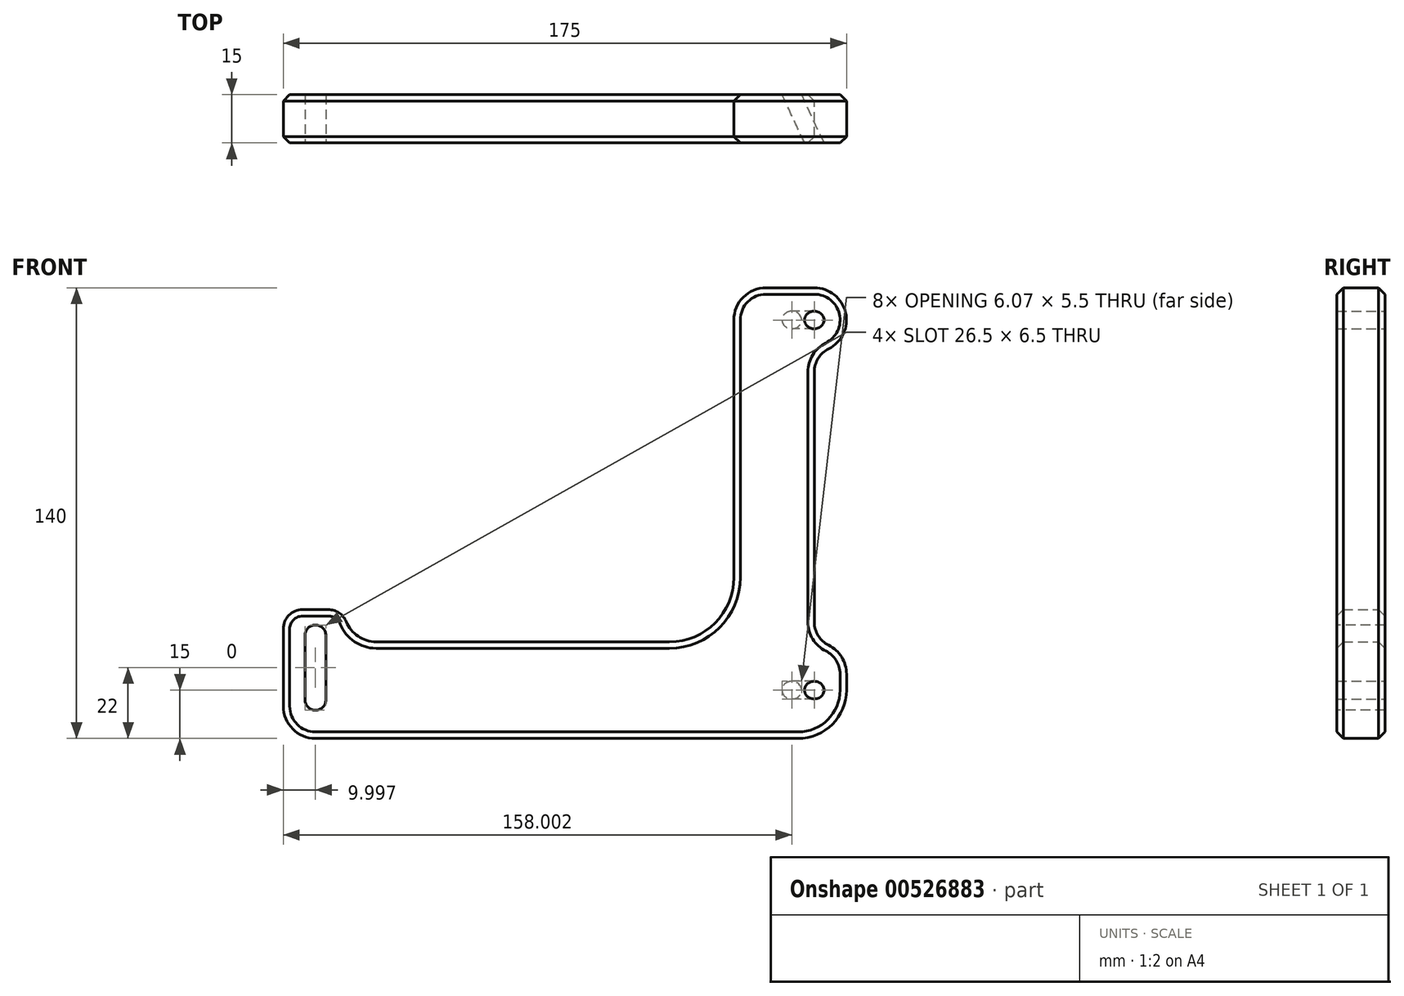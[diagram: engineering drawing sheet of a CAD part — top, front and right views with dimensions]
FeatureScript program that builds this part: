
annotation { "Feature Type Name" : "Feature", "Feature Type Description" : "" }
export const myFeature = defineFeature(function(context is Context, id is Id, definition is map)
    precondition{}
    {
        {
            var Q0;
            Q0=qCreatedBy(makeId("Front.planeOp"),FACE);
            var sketch = newSketch(context, id + "F0", { "sketchPlane" : qUnion([Q0])});
            skLineSegment(sketch, "E0", {"start": v(-2.83, 90) * mm, "end": v(-2.83, 0) * mm});
            skLineSegment(sketch, "E1", {"start": v(-2.84, 110) * mm, "end": v(-17.83, 110) * mm});
            skLineSegment(sketch, "E2", {"start": v(-27.83, 100) * mm, "end": v(-27.83, 20) * mm});
            skLineSegment(sketch, "E3", {"start": v(-47.83, 0) * mm, "end": v(-147.83, 0) * mm});
            skLineSegment(sketch, "E4", {"start": v(-153.83, 10) * mm, "end": v(-161.83, 10) * mm});
            skLineSegment(sketch, "E5", {"start": v(-167.83, 4) * mm, "end": v(-167.83, -20) * mm});
            skLineSegment(sketch, "E6", {"start": v(-157.83, -30) * mm, "end": v(-7.83, -30) * mm});
            skLineSegment(sketch, "E7", {"start": v(7.17, -15) * mm, "end": v(7.17, -10) * mm});
            skLineSegment(sketch, "E8", {"start": v(-2.83, 0) * mm, "end": v(-2.83, 0) * mm});
            skPoint(sketch, "E9.visualSharp", {"position": v(-27.83, 110) * mm});
            skArc(sketch, "E9.filletArc", {"start": v(-17.83, 110) * mm, "mid": v(-24.9, 107.07) * mm, "end": v(-27.83, 100) * mm});
            skPoint(sketch, "E10.visualSharp", {"position": v(7.16, 110) * mm});
            skLineSegment(sketch, "E10.filletArc", {"start": v(7.16, 110) * mm, "end": v(7.16, 110) * mm});
            skPoint(sketch, "E11.visualSharp", {"position": v(7.16, 90) * mm});
            skPoint(sketch, "E12.visualSharp", {"position": v(-2.83, 90) * mm});
            skPoint(sketch, "E13.visualSharp", {"position": v(-2.83, 0) * mm});
            skPoint(sketch, "E14.visualSharp", {"position": v(7.17, 0) * mm});
            skPoint(sketch, "E15.visualSharp", {"position": v(7.17, -30) * mm});
            skArc(sketch, "E15.filletArc", {"start": v(-7.83, -30) * mm, "mid": v(2.77, -25.6) * mm, "end": v(7.17, -15) * mm});
            skPoint(sketch, "E16.visualSharp", {"position": v(-27.83, 0) * mm});
            skArc(sketch, "E16.filletArc", {"start": v(-47.83, 0) * mm, "mid": v(-33.7, 5.86) * mm, "end": v(-27.83, 20) * mm});
            skPoint(sketch, "E17.visualSharp", {"position": v(-147.83, 0) * mm});
            skPoint(sketch, "E18.visualSharp", {"position": v(-147.83, 10) * mm});
            skPoint(sketch, "E19.visualSharp", {"position": v(-167.83, 10) * mm});
            skArc(sketch, "E19.filletArc", {"start": v(-161.83, 10) * mm, "mid": v(-166.08, 8.24) * mm, "end": v(-167.83, 4) * mm});
            skPoint(sketch, "E20.visualSharp", {"position": v(-167.83, -30) * mm});
            skArc(sketch, "E20.filletArc", {"start": v(-167.83, -20) * mm, "mid": v(-164.9, -27.07) * mm, "end": v(-157.83, -30) * mm});
            skLineSegment(sketch, "E21", {"start": v(-147.83, 4) * mm, "end": v(-147.83, 4) * mm});
            skLineSegment(sketch, "E22", {"start": v(-2.84, 90) * mm, "end": v(-2.83, 90) * mm});
            skLineSegment(sketch, "E23", {"start": v(7.16, 100) * mm, "end": v(7.16, 100) * mm});
            skArc(sketch, "E24.filletArc", {"start": v(7.17, -10) * mm, "mid": v(4.24, -2.93) * mm, "end": v(-2.83, 0) * mm});
            skArc(sketch, "E25.filletArc", {"start": v(-2.84, 90) * mm, "mid": v(4.23, 92.93) * mm, "end": v(7.16, 100) * mm});
            skArc(sketch, "E26.filletArc", {"start": v(7.16, 100) * mm, "mid": v(4.23, 107.07) * mm, "end": v(-2.84, 110) * mm});
            skLineSegment(sketch, "E27", {"start": v(-147.83, 0) * mm, "end": v(-147.83, 10) * mm});
            skLineSegment(sketch, "E28", {"start": v(-153.83, 10) * mm, "end": v(-147.83, 10) * mm});
            skSolve(sketch);
        }
        {
            var Q0;
            Q0=makeQuery(id+"F0.imprint","IMPRINT",FACE,{"disambiguationData":[TD([[makeQuery(id+"F0.imprint","IMPRINT",EDGE,{"derivedFrom":sQuery(id+"F0.wireOp",EDGE,"E0")}),-1.0]])]});
            extrude(context, id + "F1", {"entities" : qUnion([Q0]), "depth" : 15 * mm, "offsetDistance" : 25 * mm});
        }
        {
            var Q0;
            Q0=makeQuery(id+"F1.opExtrude","CAP_FACE",FACE,{"disambiguationData":[OSD([sQuery(id+"F0.wireOp",EDGE,"E0"),sQuery(id+"F0.wireOp",EDGE,"J42z8YOY-xz5I-P0zV-WpF7-1QvDG5DtMwlX"),sQuery(id+"F0.wireOp",EDGE,"2vvke65l-5Rt1-P847-MWuo-q8DSQjlYU5eZ"),sQuery(id+"F0.wireOp",EDGE,"E1"),sQuery(id+"F0.wireOp",EDGE,"E2"),sQuery(id+"F0.wireOp",EDGE,"E3"),sQuery(id+"F0.wireOp",EDGE,"E4"),sQuery(id+"F0.wireOp",EDGE,"E5"),sQuery(id+"F0.wireOp",EDGE,"E6"),sQuery(id+"F0.wireOp",EDGE,"E7"),sQuery(id+"F0.wireOp",EDGE,"E8"),sQuery(id+"F0.wireOp",EDGE,"E9.filletArc"),sQuery(id+"F0.wireOp",EDGE,"E10.filletArc"),sQuery(id+"F0.wireOp",EDGE,"E11.filletArc"),sQuery(id+"F0.wireOp",EDGE,"E12.filletArc"),sQuery(id+"F0.wireOp",EDGE,"E13.filletArc"),sQuery(id+"F0.wireOp",EDGE,"E14.filletArc"),sQuery(id+"F0.wireOp",EDGE,"E15.filletArc"),sQuery(id+"F0.wireOp",EDGE,"E16.filletArc"),sQuery(id+"F0.wireOp",EDGE,"E19.filletArc"),sQuery(id+"F0.wireOp",EDGE,"E20.filletArc"),sQuery(id+"F0.wireOp",EDGE,"E21"),sQuery(id+"F0.wireOp",EDGE,"44b101ba-7efd-4e18-aab7-cb58494b7f6b.filletArc"),sQuery(id+"F0.wireOp",EDGE,"d437f479-9b5c-4e56-8808-f89f6181e417.filletArc")])],"isStart":false});
            var sketch = newSketch(context, id + "F2", { "sketchPlane" : qUnion([Q0])});
            skArc(sketch, "E29", {"start": v(-154.58, 2) * mm, "mid": v(-157.83, 5.25) * mm, "end": v(-161.08, 2) * mm});
            skArc(sketch, "E30", {"start": v(-161.08, -18) * mm, "mid": v(-157.83, -21.25) * mm, "end": v(-154.58, -18) * mm});
            skLineSegment(sketch, "E31", {"start": v(-161.08, 2) * mm, "end": v(-161.08, -18) * mm});
            skLineSegment(sketch, "E32", {"start": v(-154.58, 2) * mm, "end": v(-154.58, -18) * mm});
            skSolve(sketch);
        }
        {
            var Q0;
            Q0 = qSketchRegion(id + "F2", true);
            extrude(context, id + "F3", {"entities" : qUnion([Q0]), "operationType" : NewBodyOperationType.REMOVE, "oppositeDirection" : true, "depth" : 20 * mm, "offsetDistance" : 25 * mm});
        }
        {
            var Q0;
            Q0=makeQuery(id+"F1.opExtrude","CAP_FACE",FACE,{"disambiguationData":[OSD([sQuery(id+"F0.wireOp",EDGE,"E0"),sQuery(id+"F0.wireOp",EDGE,"J42z8YOY-xz5I-P0zV-WpF7-1QvDG5DtMwlX"),sQuery(id+"F0.wireOp",EDGE,"2vvke65l-5Rt1-P847-MWuo-q8DSQjlYU5eZ"),sQuery(id+"F0.wireOp",EDGE,"E1"),sQuery(id+"F0.wireOp",EDGE,"E2"),sQuery(id+"F0.wireOp",EDGE,"E3"),sQuery(id+"F0.wireOp",EDGE,"E4"),sQuery(id+"F0.wireOp",EDGE,"E5"),sQuery(id+"F0.wireOp",EDGE,"E6"),sQuery(id+"F0.wireOp",EDGE,"E7"),sQuery(id+"F0.wireOp",EDGE,"E8"),sQuery(id+"F0.wireOp",EDGE,"E9.filletArc"),sQuery(id+"F0.wireOp",EDGE,"E10.filletArc"),sQuery(id+"F0.wireOp",EDGE,"E11.filletArc"),sQuery(id+"F0.wireOp",EDGE,"E12.filletArc"),sQuery(id+"F0.wireOp",EDGE,"E13.filletArc"),sQuery(id+"F0.wireOp",EDGE,"E14.filletArc"),sQuery(id+"F0.wireOp",EDGE,"E15.filletArc"),sQuery(id+"F0.wireOp",EDGE,"E16.filletArc"),sQuery(id+"F0.wireOp",EDGE,"E19.filletArc"),sQuery(id+"F0.wireOp",EDGE,"E20.filletArc"),sQuery(id+"F0.wireOp",EDGE,"44b101ba-7efd-4e18-aab7-cb58494b7f6b.filletArc"),sQuery(id+"F0.wireOp",EDGE,"d437f479-9b5c-4e56-8808-f89f6181e417.filletArc")])],"isStart":false});
            var sketch = newSketch(context, id + "F4", { "sketchPlane" : qUnion([Q0])});
            skCircle(sketch, "E33", {"center": v(-2.83, 100) * mm, "radius": 3 * mm});
            skCircle(sketch, "E34", {"center": v(-2.83, -15) * mm, "radius": 3 * mm});
            skSolve(sketch);
        }
        {
            var Q0;
            Q0=makeQuery(id+"F1.opExtrude","CAP_EDGE",EDGE,{"disambiguationData":[OSD([sQuery(id+"F0.wireOp",EDGE,"E2")])],"isStart":false});
            cPlane(context, id + "F5", {"entities" : qUnion([Q0]), "cplaneType" : CPlaneType.LINE_ANGLE, "offset" : 25 * mm, "angle" : 65 * degree, "width" : 150 * mm, "height" : 150 * mm});
        }
        {
            var Q0;
            Q0=qCreatedBy(id+"F5.planeOp",FACE);
            cPlane(context, id + "F6", {"entities" : qUnion([Q0]), "cplaneType" : CPlaneType.OFFSET, "offset" : 25 * mm, "width" : 150 * mm, "height" : 150 * mm});
        }
        {
            var Q0;
            Q0=qCreatedBy(id+"F6.planeOp",FACE);
            var sketch = newSketch(context, id + "F7", { "sketchPlane" : qUnion([Q0])});
            skPoint(sketch, "E35.0", {"position": v(8.9, 100) * mm});
            skPoint(sketch, "E36.0", {"position": v(8.9, -15) * mm});
            skSolve(sketch);
        }
        {
            var Q0;
            Q0=sQuery(id+"F7.wireOp",VERTEX,"E35.0");
            var Q1;
            Q1=sQuery(id+"F7.wireOp",VERTEX,"E36.0");
            var Q2;
            Q2=makeQuery(id+"F1.opExtrude","SWEPT_BODY",BODY,{"disambiguationData":[OSD([sQuery(id+"F0.wireOp",EDGE,"E0"),sQuery(id+"F0.wireOp",EDGE,"J42z8YOY-xz5I-P0zV-WpF7-1QvDG5DtMwlX"),sQuery(id+"F0.wireOp",EDGE,"2vvke65l-5Rt1-P847-MWuo-q8DSQjlYU5eZ"),sQuery(id+"F0.wireOp",EDGE,"E1"),sQuery(id+"F0.wireOp",EDGE,"E2"),sQuery(id+"F0.wireOp",EDGE,"E3"),sQuery(id+"F0.wireOp",EDGE,"E4"),sQuery(id+"F0.wireOp",EDGE,"E5"),sQuery(id+"F0.wireOp",EDGE,"E6"),sQuery(id+"F0.wireOp",EDGE,"E7"),sQuery(id+"F0.wireOp",EDGE,"E8"),sQuery(id+"F0.wireOp",EDGE,"E9.filletArc"),sQuery(id+"F0.wireOp",EDGE,"E10.filletArc"),sQuery(id+"F0.wireOp",EDGE,"E11.filletArc"),sQuery(id+"F0.wireOp",EDGE,"E12.filletArc"),sQuery(id+"F0.wireOp",EDGE,"E13.filletArc"),sQuery(id+"F0.wireOp",EDGE,"E14.filletArc"),sQuery(id+"F0.wireOp",EDGE,"E15.filletArc"),sQuery(id+"F0.wireOp",EDGE,"E16.filletArc"),sQuery(id+"F0.wireOp",EDGE,"E19.filletArc"),sQuery(id+"F0.wireOp",EDGE,"E20.filletArc"),sQuery(id+"F0.wireOp",EDGE,"44b101ba-7efd-4e18-aab7-cb58494b7f6b.filletArc"),sQuery(id+"F0.wireOp",EDGE,"d437f479-9b5c-4e56-8808-f89f6181e417.filletArc")])]});
            hole(context, id + "F8", {"style" : HoleStyle.SIMPLE, "endStyle" : HoleEndStyle.THROUGH, "standardTappedOrClearance" : lookupTablePath({ "standard" : "ISO", "fit" : "Normal", "size" : "M5", "type" : "Clearance" }), "standardBlindInLast" : lookupTablePath({ "fit" : "Standard", "standard" : "ISO", "size" : "M5", "type" : "Clearance" }), "holeDiameter" : 5.5 * mm, "isTappedThrough" : true, "tappedDepth" : 12 * mm, "tapClearance" : 3, "locations" : qUnion([Q0, Q1]), "scope" : qUnion([Q2])});
        }
        {
            var Q0;
            Q0=makeQuery(id+"F1.opExtrude","SWEPT_EDGE",EDGE,{"disambiguationData":[OSD([sQuery(id+"F0.wireOp",EDGE,"E0"),sQuery(id+"F0.wireOp",EDGE,"E24.filletArc")])]});
            var Q1;
            Q1=makeQuery(id+"F1.opExtrude","SWEPT_EDGE",EDGE,{"disambiguationData":[OSD([sQuery(id+"F0.wireOp",EDGE,"E0"),sQuery(id+"F0.wireOp",EDGE,"E25.filletArc")])]});
            fillet(context, id + "F9", {"entities" : qUnion([Q0, Q1]), "radius" : 8 * mm, "tangentPropagation" : true, "allowEdgeOverflow" : false});
        }
        {
            var Q0;
            Q0=makeQuery(id+"F1.opExtrude","SWEPT_EDGE",EDGE,{"disambiguationData":[OSD([sQuery(id+"F0.wireOp",EDGE,"E27"),sQuery(id+"F0.wireOp",EDGE,"E28")])]});
            fillet(context, id + "F10", {"entities" : qUnion([Q0]), "radius" : 6 * mm, "tangentPropagation" : true, "allowEdgeOverflow" : false});
        }
        {
            var Q0;
            Q0=makeQuery(id+"F1.opExtrude","SWEPT_EDGE",EDGE,{"disambiguationData":[OSD([sQuery(id+"F0.wireOp",EDGE,"E3"),sQuery(id+"F0.wireOp",EDGE,"E27")])]});
            fillet(context, id + "F11", {"entities" : qUnion([Q0]), "radius" : 10 * mm, "tangentPropagation" : true, "allowEdgeOverflow" : false});
        }
        {
            var Q0;
            Q0=makeQuery(id+"F1.opExtrude","CAP_EDGE",EDGE,{"disambiguationData":[OSD([sQuery(id+"F0.wireOp",EDGE,"E3")])],"isStart":false});
            var Q1;
            Q1=makeQuery(id+"F1.opExtrude","CAP_EDGE",EDGE,{"disambiguationData":[OSD([sQuery(id+"F0.wireOp",EDGE,"E3")])],"isStart":true});
            chamfer(context, id + "F12", {"entities" : qUnion([Q0, Q1]), "width" : 2 * mm, "tangentPropagation" : true});
        }
    });
